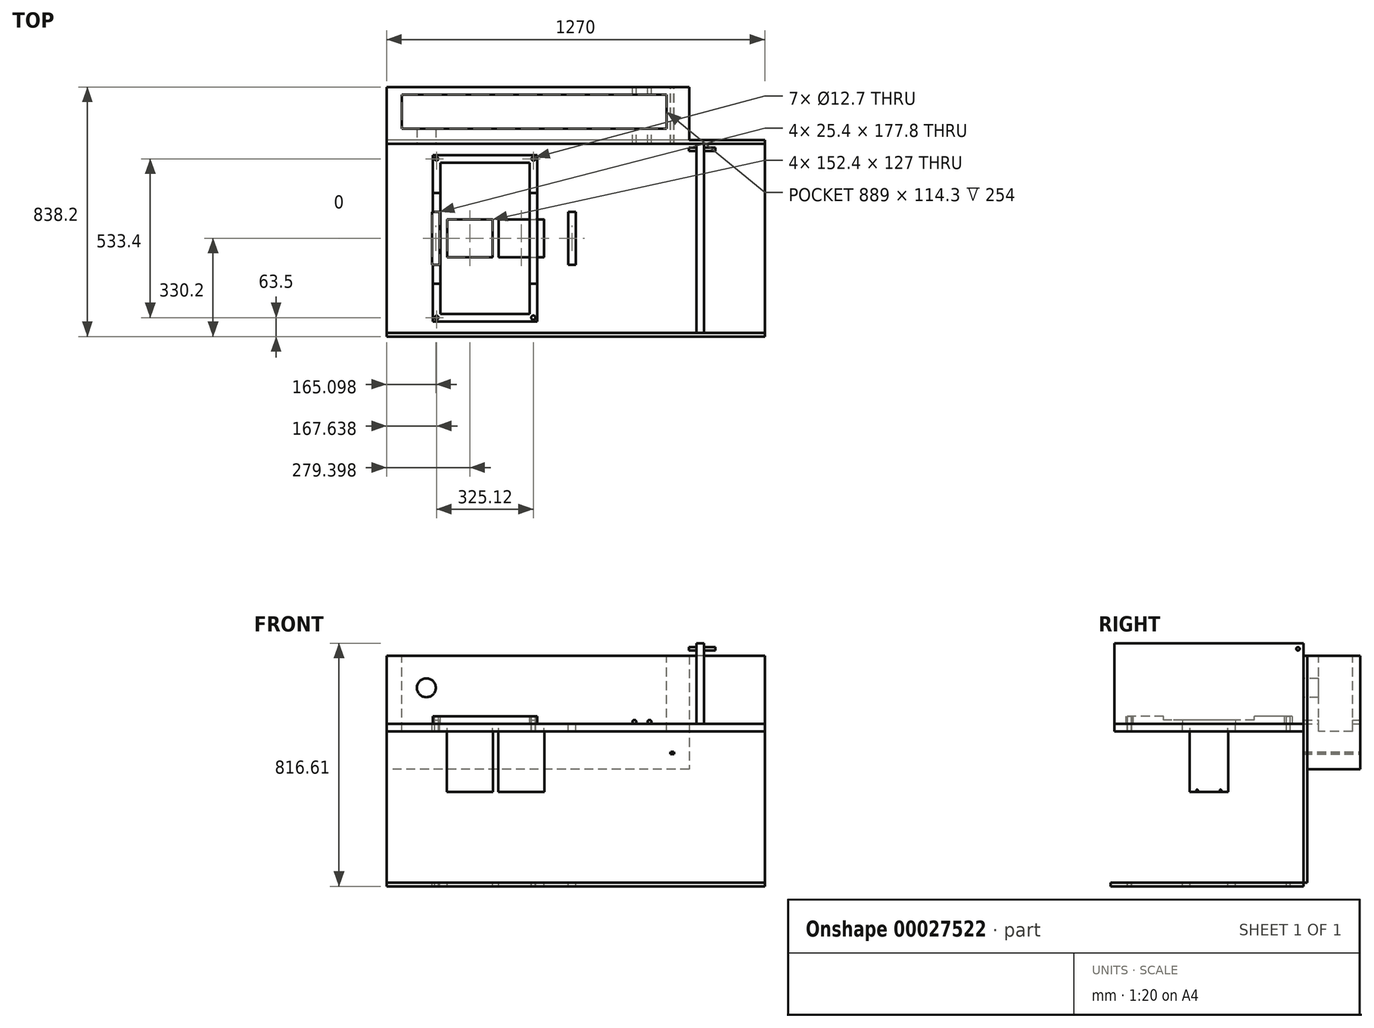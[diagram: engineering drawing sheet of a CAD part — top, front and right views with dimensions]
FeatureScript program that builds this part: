
annotation { "Feature Type Name" : "Feature", "Feature Type Description" : "" }
export const myFeature = defineFeature(function(context is Context, id is Id, definition is map)
    precondition{}
    {
        {
            var Q0;
            Q0=qCreatedBy(makeId("Front.planeOp"),FACE);
            var sketch = newSketch(context, id + "F0", { "sketchPlane" : qUnion([Q0])});
            skLineSegment(sketch, "E0.bottom", {"start": v(597.35, 481.93) * mm, "end": v(-672.65, 481.93) * mm});
            skLineSegment(sketch, "E0.top", {"start": v(597.35, -280.07) * mm, "end": v(-672.65, -280.07) * mm});
            skLineSegment(sketch, "E0.left", {"start": v(597.35, 481.93) * mm, "end": v(597.35, -280.07) * mm});
            skLineSegment(sketch, "E0.right", {"start": v(-672.65, 481.93) * mm, "end": v(-672.65, -280.07) * mm});
            skSolve(sketch);
        }
        {
            var Q0;
            Q0=makeQuery(id+"F0.imprint","IMPRINT",FACE,{"disambiguationData":[TD([[makeQuery(id+"F0.imprint","IMPRINT",EDGE,{"derivedFrom":sQuery(id+"F0.wireOp",EDGE,"E0.bottom")}),1.0]])]});
            extrude(context, id + "F1", {"entities" : qUnion([Q0]), "depth" : 12.7 * mm});
        }
        {
            var Q0;
            Q0=makeQuery(id+"F1.opExtrude","CAP_FACE",FACE,{"disambiguationData":[OSD([sQuery(id+"F0.wireOp",EDGE,"E0.bottom"),sQuery(id+"F0.wireOp",EDGE,"E0.top"),sQuery(id+"F0.wireOp",EDGE,"E0.left"),sQuery(id+"F0.wireOp",EDGE,"E0.right")])],"isStart":false});
            var sketch = newSketch(context, id + "F2", { "sketchPlane" : qUnion([Q0])});
            skLineSegment(sketch, "E1", {"start": v(-672.65, 253.33) * mm, "end": v(597.35, 253.33) * mm});
            skLineSegment(sketch, "E2", {"start": v(597.35, 253.33) * mm, "end": v(597.35, 227.93) * mm});
            skLineSegment(sketch, "E3", {"start": v(597.35, 227.93) * mm, "end": v(-672.65, 227.93) * mm});
            skLineSegment(sketch, "E4", {"start": v(-672.65, 227.93) * mm, "end": v(-672.65, 253.33) * mm});
            skSolve(sketch);
        }
        {
            var Q0;
            Q0=makeQuery(id+"F2.imprint","IMPRINT",FACE,{"disambiguationData":[TD([[makeQuery(id+"F2.imprint","IMPRINT",EDGE,{"derivedFrom":sQuery(id+"F2.wireOp",EDGE,"E1")}),-1.0]])]});
            extrude(context, id + "F3", {"entities" : qUnion([Q0]), "depth" : 635 * mm});
        }
        {
            var Q0;
            Q0=makeQuery(id+"F3.opExtrude","SWEPT_FACE",FACE,{"disambiguationData":[OSD([sQuery(id+"F2.wireOp",EDGE,"E1")])]});
            var sketch = newSketch(context, id + "F4", { "sketchPlane" : qUnion([Q0])});
            skLineSegment(sketch, "E5.bottom", {"start": v(367.14, -12.7) * mm, "end": v(392.54, -12.7) * mm});
            skLineSegment(sketch, "E5.top", {"start": v(367.14, -647.7) * mm, "end": v(392.54, -647.7) * mm});
            skLineSegment(sketch, "E5.left", {"start": v(367.14, -12.7) * mm, "end": v(367.14, -647.7) * mm});
            skLineSegment(sketch, "E5.right", {"start": v(392.54, -12.7) * mm, "end": v(392.54, -647.7) * mm});
            skSolve(sketch);
        }
        {
            var Q0;
            Q0=makeQuery(id+"F4.imprint","IMPRINT",FACE,{"disambiguationData":[TD([[makeQuery(id+"F4.imprint","IMPRINT",EDGE,{"derivedFrom":sQuery(id+"F4.wireOp",EDGE,"E5.bottom")}),-1.0]])]});
            extrude(context, id + "F5", {"entities" : qUnion([Q0]), "depth" : 270.5 * mm});
        }
        {
            var Q0;
            Q0=makeQuery(id+"F1.opExtrude","CAP_FACE",FACE,{"disambiguationData":[OSD([sQuery(id+"F0.wireOp",EDGE,"E0.bottom"),sQuery(id+"F0.wireOp",EDGE,"E0.top"),sQuery(id+"F0.wireOp",EDGE,"E0.left"),sQuery(id+"F0.wireOp",EDGE,"E0.right")])],"isStart":true});
            var sketch = newSketch(context, id + "F6", { "sketchPlane" : qUnion([Q0])});
            skLineSegment(sketch, "E6.bottom", {"start": v(-343.35, 481.93) * mm, "end": v(672.65, 481.93) * mm});
            skLineSegment(sketch, "E6.top", {"start": v(-343.35, 100.93) * mm, "end": v(672.65, 100.93) * mm});
            skLineSegment(sketch, "E6.left", {"start": v(-343.35, 481.93) * mm, "end": v(-343.35, 100.93) * mm});
            skLineSegment(sketch, "E6.right", {"start": v(672.65, 481.93) * mm, "end": v(672.65, 100.93) * mm});
            skSolve(sketch);
        }
        {
            var Q0;
            Q0=makeQuery(id+"F6.imprint","IMPRINT",FACE,{"disambiguationData":[TD([[makeQuery(id+"F6.imprint","IMPRINT",EDGE,{"derivedFrom":sQuery(id+"F6.wireOp",EDGE,"E6.bottom")}),-1.0]])]});
            extrude(context, id + "F7", {"entities" : qUnion([Q0]), "operationType" : NewBodyOperationType.ADD, "depth" : 177.8 * mm});
        }
        {
            var Q0;
            Q0=makeQuery(id+"F7.boolean.opBoolean","MERGE",FACE,{"derivedFrom":[makeQuery(id+"F1.opExtrude","SWEPT_FACE",FACE,{"disambiguationData":[OSD([sQuery(id+"F0.wireOp",EDGE,"E0.bottom")])]}),makeQuery(id+"F7.opExtrude","SWEPT_FACE",FACE,{"disambiguationData":[OSD([sQuery(id+"F6.wireOp",EDGE,"E6.bottom")])]})]});
            var sketch = newSketch(context, id + "F8", { "sketchPlane" : qUnion([Q0])});
            skLineSegment(sketch, "E7.bottom", {"start": v(-621.85, 152.4) * mm, "end": v(267.15, 152.4) * mm});
            skLineSegment(sketch, "E7.top", {"start": v(-621.85, 38.1) * mm, "end": v(267.15, 38.1) * mm});
            skLineSegment(sketch, "E7.left", {"start": v(-621.85, 152.4) * mm, "end": v(-621.85, 38.1) * mm});
            skLineSegment(sketch, "E7.right", {"start": v(267.15, 152.4) * mm, "end": v(267.15, 38.1) * mm});
            skSolve(sketch);
        }
        {
            var Q0;
            Q0=makeQuery(id+"F8.imprint","IMPRINT",FACE,{"disambiguationData":[TD([[makeQuery(id+"F8.imprint","IMPRINT",EDGE,{"derivedFrom":sQuery(id+"F8.wireOp",EDGE,"E7.bottom")}),-1.0]])]});
            extrude(context, id + "F9", {"entities" : qUnion([Q0]), "operationType" : NewBodyOperationType.REMOVE, "oppositeDirection" : true, "depth" : 254 * mm});
        }
        {
            var Q0;
            Q0=makeQuery(id+"F1.opExtrude","CAP_FACE",FACE,{"disambiguationData":[OSD([sQuery(id+"F0.wireOp",EDGE,"E0.bottom"),sQuery(id+"F0.wireOp",EDGE,"E0.top"),sQuery(id+"F0.wireOp",EDGE,"E0.left"),sQuery(id+"F0.wireOp",EDGE,"E0.right")])],"isStart":false});
            var sketch = newSketch(context, id + "F10", { "sketchPlane" : qUnion([Q0])});
            skCircle(sketch, "E8", {"center": v(-539.3, 373.98) * mm, "radius": 31.75 * mm});
            skSolve(sketch);
        }
        {
            var Q0;
            Q0=makeQuery(id+"F10.imprint","IMPRINT",FACE,{"disambiguationData":[TD([[makeQuery(id+"F10.imprint","IMPRINT",EDGE,{"derivedFrom":sQuery(id+"F10.wireOp",EDGE,"E8")}),1.0]])]});
            extrude(context, id + "F11", {"entities" : qUnion([Q0]), "operationType" : NewBodyOperationType.REMOVE, "oppositeDirection" : true, "depth" : 50.8 * mm});
        }
        {
            var Q0;
            Q0=makeQuery(id+"F7.opExtrude","CAP_FACE",FACE,{"disambiguationData":[OSD([sQuery(id+"F6.wireOp",EDGE,"E6.bottom"),sQuery(id+"F6.wireOp",EDGE,"E6.top"),sQuery(id+"F6.wireOp",EDGE,"E6.left"),sQuery(id+"F6.wireOp",EDGE,"E6.right")])],"isStart":false});
            var sketch = newSketch(context, id + "F12", { "sketchPlane" : qUnion([Q0])});
            skCircle(sketch, "E9", {"center": v(-210, 259.68) * mm, "radius": 6.35 * mm});
            skCircle(sketch, "E10", {"center": v(-159.2, 259.68) * mm, "radius": 6.35 * mm});
            skLineSegment(sketch, "E11", {"start": v(-291.28, 159.01) * mm, "end": v(-281.12, 159.01) * mm});
            skLineSegment(sketch, "E12", {"start": v(-281.12, 159.01) * mm, "end": v(-279.85, 156.81) * mm});
            skLineSegment(sketch, "E13", {"start": v(-279.85, 156.81) * mm, "end": v(-279.85, 151.73) * mm});
            skLineSegment(sketch, "E14", {"start": v(-279.85, 151.73) * mm, "end": v(-292.55, 151.73) * mm});
            skLineSegment(sketch, "E15", {"start": v(-292.55, 151.73) * mm, "end": v(-292.55, 156.81) * mm});
            skLineSegment(sketch, "E16", {"start": v(-292.55, 156.81) * mm, "end": v(-291.28, 159.01) * mm});
            skSolve(sketch);
        }
        {
            var Q0;
            Q0=makeQuery(id+"F12.imprint","IMPRINT",FACE,{"disambiguationData":[TD([[makeQuery(id+"F12.imprint","IMPRINT",EDGE,{"derivedFrom":sQuery(id+"F12.wireOp",EDGE,"E9")}),1.0]])]});
            var Q1;
            Q1=makeQuery(id+"F12.imprint","IMPRINT",FACE,{"disambiguationData":[TD([[makeQuery(id+"F12.imprint","IMPRINT",EDGE,{"derivedFrom":sQuery(id+"F12.wireOp",EDGE,"E10")}),1.0]])]});
            var Q2;
            Q2=makeQuery(id+"F12.imprint","IMPRINT",FACE,{"disambiguationData":[TD([[makeQuery(id+"F12.imprint","IMPRINT",EDGE,{"derivedFrom":sQuery(id+"F12.wireOp",EDGE,"E11")}),-1.0]])]});
            extrude(context, id + "F13", {"entities" : qUnion([Q0, Q1, Q2]), "operationType" : NewBodyOperationType.REMOVE, "endBound" : BoundingType.THROUGH_ALL, "oppositeDirection" : true, "depth" : 25.4 * mm});
        }
        {
            var Q0;
            Q0=makeQuery(id+"F5.opExtrude","SWEPT_FACE",FACE,{"disambiguationData":[OSD([sQuery(id+"F4.wireOp",EDGE,"E5.left")])]});
            var sketch = newSketch(context, id + "F14", { "sketchPlane" : qUnion([Q0])});
            skCircle(sketch, "E17", {"center": v(31.12, 504.8) * mm, "radius": 5.72 * mm});
            skSolve(sketch);
        }
        {
            var Q0;
            Q0=makeQuery(id+"F14.imprint","IMPRINT",FACE,{"disambiguationData":[TD([[makeQuery(id+"F14.imprint","IMPRINT",EDGE,{"derivedFrom":sQuery(id+"F14.wireOp",EDGE,"E17")}),1.0]])]});
            extrude(context, id + "F15", {"entities" : qUnion([Q0]), "operationType" : NewBodyOperationType.ADD, "depth" : 25.4 * mm});
        }
        {
            var Q0;
            Q0=makeQuery(id+"F5.opExtrude","SWEPT_FACE",FACE,{"disambiguationData":[OSD([sQuery(id+"F4.wireOp",EDGE,"E5.right")])]});
            var sketch = newSketch(context, id + "F16", { "sketchPlane" : qUnion([Q0])});
            skCircle(sketch, "E18", {"center": v(-31.12, 504.8) * mm, "radius": 5.72 * mm});
            skSolve(sketch);
        }
        {
            var Q0;
            Q0=makeQuery(id+"F16.imprint","IMPRINT",FACE,{"disambiguationData":[TD([[makeQuery(id+"F16.imprint","IMPRINT",EDGE,{"derivedFrom":sQuery(id+"F16.wireOp",EDGE,"E18")}),1.0]])]});
            extrude(context, id + "F17", {"entities" : qUnion([Q0]), "operationType" : NewBodyOperationType.ADD, "depth" : 38.1 * mm});
        }
        {
            var Q0;
            Q0=makeQuery(id+"F1.opExtrude","CAP_FACE",FACE,{"disambiguationData":[OSD([sQuery(id+"F0.wireOp",EDGE,"E0.bottom"),sQuery(id+"F0.wireOp",EDGE,"E0.top"),sQuery(id+"F0.wireOp",EDGE,"E0.left"),sQuery(id+"F0.wireOp",EDGE,"E0.right")])],"isStart":false});
            var sketch = newSketch(context, id + "F18", { "sketchPlane" : qUnion([Q0])});
            skLineSegment(sketch, "E19.bottom", {"start": v(-672.65, -280.07) * mm, "end": v(597.35, -280.07) * mm});
            skLineSegment(sketch, "E19.top", {"start": v(-672.65, -292.77) * mm, "end": v(597.35, -292.77) * mm});
            skLineSegment(sketch, "E19.left", {"start": v(-672.65, -280.07) * mm, "end": v(-672.65, -292.77) * mm});
            skLineSegment(sketch, "E19.right", {"start": v(597.35, -280.07) * mm, "end": v(597.35, -292.77) * mm});
            skSolve(sketch);
        }
        {
            var Q0;
            Q0=makeQuery(id+"F18.imprint","IMPRINT",FACE,{"disambiguationData":[TD([[makeQuery(id+"F18.imprint","IMPRINT",EDGE,{"derivedFrom":sQuery(id+"F18.wireOp",EDGE,"E19.bottom")}),1.0]])]});
            extrude(context, id + "F19", {"entities" : qUnion([Q0]), "depth" : 647.7 * mm});
        }
        {
            var Q0;
            Q0=makeQuery(id+"F3.opExtrude","SWEPT_FACE",FACE,{"disambiguationData":[OSD([sQuery(id+"F2.wireOp",EDGE,"E1")])]});
            var sketch = newSketch(context, id + "F20", { "sketchPlane" : qUnion([Q0])});
            skLineSegment(sketch, "E20.bottom", {"start": v(-520.25, -241.3) * mm, "end": v(-494.85, -241.3) * mm});
            skLineSegment(sketch, "E20.top", {"start": v(-520.25, -419.1) * mm, "end": v(-494.85, -419.1) * mm});
            skLineSegment(sketch, "E20.left", {"start": v(-520.25, -241.3) * mm, "end": v(-520.25, -419.1) * mm});
            skLineSegment(sketch, "E20.right", {"start": v(-494.85, -241.3) * mm, "end": v(-494.85, -419.1) * mm});
            skLineSegment(sketch, "E21.bottom", {"start": v(-63.05, -241.3) * mm, "end": v(-37.65, -241.3) * mm});
            skLineSegment(sketch, "E21.top", {"start": v(-63.05, -419.1) * mm, "end": v(-37.65, -419.1) * mm});
            skLineSegment(sketch, "E21.left", {"start": v(-37.65, -241.3) * mm, "end": v(-37.65, -419.1) * mm});
            skLineSegment(sketch, "E21.right", {"start": v(-63.05, -241.3) * mm, "end": v(-63.05, -419.1) * mm});
            skSolve(sketch);
        }
        {
            var Q0;
            Q0=makeQuery(id+"F20.imprint","IMPRINT",FACE,{"disambiguationData":[TD([[makeQuery(id+"F20.imprint","IMPRINT",EDGE,{"derivedFrom":sQuery(id+"F20.wireOp",EDGE,"E20.bottom")}),-1.0]])]});
            var Q1;
            Q1=makeQuery(id+"F20.imprint","IMPRINT",FACE,{"disambiguationData":[TD([[makeQuery(id+"F20.imprint","IMPRINT",EDGE,{"derivedFrom":sQuery(id+"F20.wireOp",EDGE,"E21.bottom")}),-1.0]])]});
            extrude(context, id + "F21", {"entities" : qUnion([Q0, Q1]), "operationType" : NewBodyOperationType.REMOVE, "endBound" : BoundingType.THROUGH_ALL, "oppositeDirection" : true, "depth" : 25.4 * mm});
        }
        {
            var Q0;
            Q0=makeQuery(id+"F3.opExtrude","SWEPT_FACE",FACE,{"disambiguationData":[OSD([sQuery(id+"F2.wireOp",EDGE,"E1")])]});
            var sketch = newSketch(context, id + "F22", { "sketchPlane" : qUnion([Q0])});
            skLineSegment(sketch, "E22.bottom", {"start": v(-520.25, -38.1) * mm, "end": v(-164.65, -38.1) * mm, "construction": true});
            skLineSegment(sketch, "E22.top", {"start": v(-520.25, -622.3) * mm, "end": v(-164.65, -622.3) * mm, "construction": true});
            skLineSegment(sketch, "E22.left", {"start": v(-520.25, -38.1) * mm, "end": v(-520.25, -622.3) * mm, "construction": true});
            skLineSegment(sketch, "E22.right", {"start": v(-164.65, -38.1) * mm, "end": v(-164.65, -622.3) * mm, "construction": true});
            skLineSegment(sketch, "E23.bottom", {"start": v(-517.71, -50.8) * mm, "end": v(-167.2, -50.8) * mm});
            skLineSegment(sketch, "E23.top", {"start": v(-517.71, -609.6) * mm, "end": v(-167.2, -609.6) * mm});
            skLineSegment(sketch, "E23.left", {"start": v(-517.71, -50.8) * mm, "end": v(-517.71, -609.6) * mm});
            skLineSegment(sketch, "E23.right", {"start": v(-167.2, -50.8) * mm, "end": v(-167.2, -609.6) * mm});
            skSolve(sketch);
        }
        {
            var Q0;
            Q0=makeQuery(id+"F22.imprint","IMPRINT",FACE,{"disambiguationData":[TD([[makeQuery(id+"F22.imprint","IMPRINT",EDGE,{"derivedFrom":sQuery(id+"F22.wireOp",EDGE,"E23.bottom")}),-1.0]])]});
            extrude(context, id + "F23", {"entities" : qUnion([Q0]), "depth" : 25.4 * mm});
        }
        {
            var Q0;
            Q0=makeQuery(id+"F23.opExtrude","CAP_FACE",FACE,{"disambiguationData":[OSD([sQuery(id+"FGRaveqPXn7Mfuw_3.wireOp",EDGE,"31ecdb2b-451b-4d1c-ab21-257dd7b72239.bottom"),sQuery(id+"FGRaveqPXn7Mfuw_3.wireOp",EDGE,"31ecdb2b-451b-4d1c-ab21-257dd7b72239.top"),sQuery(id+"FGRaveqPXn7Mfuw_3.wireOp",EDGE,"31ecdb2b-451b-4d1c-ab21-257dd7b72239.left"),sQuery(id+"FGRaveqPXn7Mfuw_3.wireOp",EDGE,"31ecdb2b-451b-4d1c-ab21-257dd7b72239.right"),sQuery(id+"F22.wireOp",EDGE,"E23.bottom"),sQuery(id+"F22.wireOp",EDGE,"E23.top"),sQuery(id+"F22.wireOp",EDGE,"E23.left"),sQuery(id+"F22.wireOp",EDGE,"E23.right")])],"isStart":false});
            var sketch = newSketch(context, id + "F24", { "sketchPlane" : qUnion([Q0])});
            skLineSegment(sketch, "E24.bottom", {"start": v(-492.31, -76.2) * mm, "end": v(-192.6, -76.2) * mm});
            skLineSegment(sketch, "E24.top", {"start": v(-492.31, -584.2) * mm, "end": v(-192.6, -584.2) * mm});
            skLineSegment(sketch, "E24.left", {"start": v(-492.31, -76.2) * mm, "end": v(-492.31, -584.2) * mm});
            skLineSegment(sketch, "E24.right", {"start": v(-192.6, -76.2) * mm, "end": v(-192.6, -584.2) * mm});
            skSolve(sketch);
        }
        {
            var Q0;
            Q0=makeQuery(id+"F24.imprint","IMPRINT",FACE,{"disambiguationData":[TD([[makeQuery(id+"F24.imprint","IMPRINT",EDGE,{"derivedFrom":sQuery(id+"F24.wireOp",EDGE,"E24.bottom")}),-1.0]])]});
            extrude(context, id + "F25", {"entities" : qUnion([Q0]), "operationType" : NewBodyOperationType.REMOVE, "oppositeDirection" : true, "depth" : 25.4 * mm});
        }
        {
            var Q0;
            Q0=makeQuery(id+"F23.opExtrude","CAP_FACE",FACE,{"disambiguationData":[OSD([sQuery(id+"FGRaveqPXn7Mfuw_3.wireOp",EDGE,"31ecdb2b-451b-4d1c-ab21-257dd7b72239.bottom"),sQuery(id+"FGRaveqPXn7Mfuw_3.wireOp",EDGE,"31ecdb2b-451b-4d1c-ab21-257dd7b72239.top"),sQuery(id+"FGRaveqPXn7Mfuw_3.wireOp",EDGE,"31ecdb2b-451b-4d1c-ab21-257dd7b72239.left"),sQuery(id+"FGRaveqPXn7Mfuw_3.wireOp",EDGE,"31ecdb2b-451b-4d1c-ab21-257dd7b72239.right"),sQuery(id+"F22.wireOp",EDGE,"E23.bottom"),sQuery(id+"F22.wireOp",EDGE,"E23.top"),sQuery(id+"F22.wireOp",EDGE,"E23.left"),sQuery(id+"F22.wireOp",EDGE,"E23.right")])],"isStart":false});
            var sketch = newSketch(context, id + "F26", { "sketchPlane" : qUnion([Q0])});
            skCircle(sketch, "E25", {"center": v(-179.9, -63.5) * mm, "radius": 6.35 * mm});
            skCircle(sketch, "E26", {"center": v(-505.01, -63.5) * mm, "radius": 5.99 * mm});
            skCircle(sketch, "E27", {"center": v(-505.01, -596.9) * mm, "radius": 6.35 * mm});
            skCircle(sketch, "E28", {"center": v(-179.9, -596.9) * mm, "radius": 7.2 * mm});
            skSolve(sketch);
        }
        {
            var Q0;
            Q0=makeQuery(id+"F26.imprint","IMPRINT",FACE,{"disambiguationData":[TD([[makeQuery(id+"F26.imprint","IMPRINT",EDGE,{"derivedFrom":sQuery(id+"F26.wireOp",EDGE,"E27")}),1.0]])]});
            var Q1;
            Q1=makeQuery(id+"F26.imprint","IMPRINT",FACE,{"disambiguationData":[TD([[makeQuery(id+"F26.imprint","IMPRINT",EDGE,{"derivedFrom":sQuery(id+"F26.wireOp",EDGE,"E28")}),1.0]])]});
            var Q2;
            Q2=makeQuery(id+"F26.imprint","IMPRINT",FACE,{"disambiguationData":[TD([[makeQuery(id+"F26.imprint","IMPRINT",EDGE,{"derivedFrom":sQuery(id+"F26.wireOp",EDGE,"E25")}),1.0]])]});
            var Q3;
            Q3=makeQuery(id+"F26.imprint","IMPRINT",FACE,{"disambiguationData":[TD([[makeQuery(id+"F26.imprint","IMPRINT",EDGE,{"derivedFrom":sQuery(id+"F26.wireOp",EDGE,"E26")}),1.0]])]});
            extrude(context, id + "F27", {"entities" : qUnion([Q0, Q1, Q2, Q3]), "operationType" : NewBodyOperationType.REMOVE, "endBound" : BoundingType.THROUGH_ALL, "oppositeDirection" : true, "depth" : 25.4 * mm});
        }
        {
            var Q0;
            Q0=makeQuery(id+"F3.opExtrude","SWEPT_FACE",FACE,{"disambiguationData":[OSD([sQuery(id+"F2.wireOp",EDGE,"E1")])]});
            var sketch = newSketch(context, id + "F28", { "sketchPlane" : qUnion([Q0])});
            skCircle(sketch, "E29", {"center": v(-505.01, -596.9) * mm, "radius": 6.35 * mm});
            skCircle(sketch, "E30", {"center": v(-179.9, -63.5) * mm, "radius": 6.35 * mm});
            skCircle(sketch, "E31", {"center": v(-505.01, -63.5) * mm, "radius": 6.35 * mm});
            skCircle(sketch, "E32", {"center": v(-179.9, -596.9) * mm, "radius": 6.35 * mm});
            skSolve(sketch);
        }
        {
            var Q0;
            Q0=sQuery(id+"F28.wireOp",VERTEX,"E29.center");
            var Q1;
            Q1=sQuery(id+"F28.wireOp",VERTEX,"E32.center");
            var Q2;
            Q2=sQuery(id+"F28.wireOp",VERTEX,"E31.center");
            var Q3;
            Q3=sQuery(id+"F28.wireOp",VERTEX,"E30.center");
            var Q4;
            Q4=makeQuery(id+"F3.opExtrude","SWEPT_BODY",BODY,{"disambiguationData":[OSD([sQuery(id+"F2.wireOp",EDGE,"E1"),sQuery(id+"F2.wireOp",EDGE,"E2"),sQuery(id+"F2.wireOp",EDGE,"E3"),sQuery(id+"F2.wireOp",EDGE,"E4")])]});
            hole(context, id + "F29", {"style" : HoleStyle.C_SINK, "holeDiameter" : 12.7 * mm, "cSinkDiameter" : 12.7 * mm, "endStyle" : HoleEndStyle.THROUGH, "locations" : qUnion([Q0, Q1, Q2, Q3]), "scope" : qUnion([Q4]), "cSinkAngle" : 90 * degree});
        }
        {
            var Q0;
            Q0=makeQuery(id+"F3.opExtrude","SWEPT_FACE",FACE,{"disambiguationData":[OSD([sQuery(id+"F2.wireOp",EDGE,"E3")])]});
            var sketch = newSketch(context, id + "F30", { "sketchPlane" : qUnion([Q0])});
            skLineSegment(sketch, "E33.bottom", {"start": v(-143.06, 265.43) * mm, "end": v(-298, 265.43) * mm});
            skLineSegment(sketch, "E33.top", {"start": v(-143.06, 394.97) * mm, "end": v(-298, 394.97) * mm});
            skLineSegment(sketch, "E33.left", {"start": v(-143.06, 265.43) * mm, "end": v(-143.06, 394.97) * mm});
            skLineSegment(sketch, "E33.right", {"start": v(-298, 265.43) * mm, "end": v(-298, 394.97) * mm});
            skLineSegment(sketch, "E34.bottom", {"start": v(-315.78, 265.43) * mm, "end": v(-470.72, 265.43) * mm});
            skLineSegment(sketch, "E34.top", {"start": v(-315.78, 394.97) * mm, "end": v(-470.72, 394.97) * mm});
            skLineSegment(sketch, "E34.left", {"start": v(-315.78, 265.43) * mm, "end": v(-315.78, 394.97) * mm});
            skLineSegment(sketch, "E34.right", {"start": v(-470.72, 265.43) * mm, "end": v(-470.72, 394.97) * mm});
            skSolve(sketch);
        }
        {
            var Q0;
            Q0 = qSketchRegion(id + "F30", true);
            extrude(context, id + "F31", {"entities" : qUnion([Q0]), "operationType" : NewBodyOperationType.ADD, "depth" : 203.2 * mm});
        }
        {
            var Q0;
            Q0=makeQuery(id+"F3.opExtrude","SWEPT_FACE",FACE,{"disambiguationData":[OSD([sQuery(id+"F2.wireOp",EDGE,"E1")])]});
            var sketch = newSketch(context, id + "F32", { "sketchPlane" : qUnion([Q0])});
            skLineSegment(sketch, "E35.bottom", {"start": v(-469.45, -266.7) * mm, "end": v(-317.05, -266.7) * mm});
            skLineSegment(sketch, "E35.top", {"start": v(-469.45, -393.7) * mm, "end": v(-317.05, -393.7) * mm});
            skLineSegment(sketch, "E35.left", {"start": v(-469.45, -266.7) * mm, "end": v(-469.45, -393.7) * mm});
            skLineSegment(sketch, "E35.right", {"start": v(-317.05, -266.7) * mm, "end": v(-317.05, -393.7) * mm});
            skLineSegment(sketch, "E36.bottom", {"start": v(-296.73, -266.7) * mm, "end": v(-144.33, -266.7) * mm});
            skLineSegment(sketch, "E36.top", {"start": v(-296.73, -393.7) * mm, "end": v(-144.33, -393.7) * mm});
            skLineSegment(sketch, "E36.left", {"start": v(-296.73, -266.7) * mm, "end": v(-296.73, -393.7) * mm});
            skLineSegment(sketch, "E36.right", {"start": v(-144.33, -266.7) * mm, "end": v(-144.33, -393.7) * mm});
            skSolve(sketch);
        }
        {
            var Q0;
            Q0 = qSketchRegion(id + "F32", true);
            extrude(context, id + "F33", {"entities" : qUnion([Q0]), "operationType" : NewBodyOperationType.REMOVE, "endBound" : BoundingType.THROUGH_ALL, "oppositeDirection" : true, "depth" : 25.4 * mm});
        }
        {
            var Q0;
            Q0=makeQuery(id+"F23.opExtrude","CAP_FACE",FACE,{"disambiguationData":[OSD([sQuery(id+"F22.wireOp",EDGE,"E23.bottom"),sQuery(id+"F22.wireOp",EDGE,"E23.top"),sQuery(id+"F22.wireOp",EDGE,"E23.left"),sQuery(id+"F22.wireOp",EDGE,"E23.right")])],"isStart":false});
            var sketch = newSketch(context, id + "F34", { "sketchPlane" : qUnion([Q0])});
            skLineSegment(sketch, "E37.bottom", {"start": v(-517.71, -177.8) * mm, "end": v(-492.31, -177.8) * mm});
            skLineSegment(sketch, "E37.top", {"start": v(-517.71, -482.6) * mm, "end": v(-492.31, -482.6) * mm});
            skLineSegment(sketch, "E37.left", {"start": v(-517.71, -177.8) * mm, "end": v(-517.71, -482.6) * mm});
            skLineSegment(sketch, "E37.right", {"start": v(-492.31, -177.8) * mm, "end": v(-492.31, -482.6) * mm});
            skLineSegment(sketch, "E38.bottom", {"start": v(-192.6, -177.8) * mm, "end": v(-167.2, -177.8) * mm});
            skLineSegment(sketch, "E38.top", {"start": v(-192.6, -482.6) * mm, "end": v(-167.2, -482.6) * mm});
            skLineSegment(sketch, "E38.left", {"start": v(-192.6, -177.8) * mm, "end": v(-192.6, -482.6) * mm});
            skLineSegment(sketch, "E38.right", {"start": v(-167.2, -177.8) * mm, "end": v(-167.2, -482.6) * mm});
            skSolve(sketch);
        }
        {
            var Q0;
            Q0=makeQuery(id+"F34.imprint","IMPRINT",FACE,{"disambiguationData":[TD([[makeQuery(id+"F34.imprint","IMPRINT",EDGE,{"derivedFrom":sQuery(id+"F34.wireOp",EDGE,"E37.bottom")}),-1.0]])]});
            var Q1;
            Q1=makeQuery(id+"F34.imprint","IMPRINT",FACE,{"disambiguationData":[TD([[makeQuery(id+"F34.imprint","IMPRINT",EDGE,{"derivedFrom":sQuery(id+"F34.wireOp",EDGE,"E38.bottom")}),-1.0]])]});
            extrude(context, id + "F35", {"entities" : qUnion([Q0, Q1]), "operationType" : NewBodyOperationType.REMOVE, "oppositeDirection" : true, "depth" : 12.7 * mm});
        }
        {
            var Q0;
            Q0=makeQuery(id+"F31.opExtrude","SWEPT_FACE",FACE,{"disambiguationData":[OSD([sQuery(id+"F30.wireOp",EDGE,"E34.right")])]});
            var sketch = newSketch(context, id + "F36", { "sketchPlane" : qUnion([Q0])});
            skCircle(sketch, "E39", {"center": v(290.83, 29.81) * mm, "radius": 2.38 * mm});
            skCircle(sketch, "E40", {"center": v(369.57, 29.81) * mm, "radius": 2.38 * mm});
            skSolve(sketch);
        }
        {
            var Q0;
            Q0=makeQuery(id+"F36.imprint","IMPRINT",FACE,{"disambiguationData":[TD([[makeQuery(id+"F36.imprint","IMPRINT",EDGE,{"derivedFrom":sQuery(id+"F36.wireOp",EDGE,"E39")}),1.0]])]});
            var Q1;
            Q1=makeQuery(id+"F36.imprint","IMPRINT",FACE,{"disambiguationData":[TD([[makeQuery(id+"F36.imprint","IMPRINT",EDGE,{"derivedFrom":sQuery(id+"F36.wireOp",EDGE,"E40")}),1.0]])]});
            extrude(context, id + "F37", {"entities" : qUnion([Q0, Q1]), "operationType" : NewBodyOperationType.REMOVE, "endBound" : BoundingType.THROUGH_ALL, "oppositeDirection" : true, "depth" : 25.4 * mm});
        }
    });
